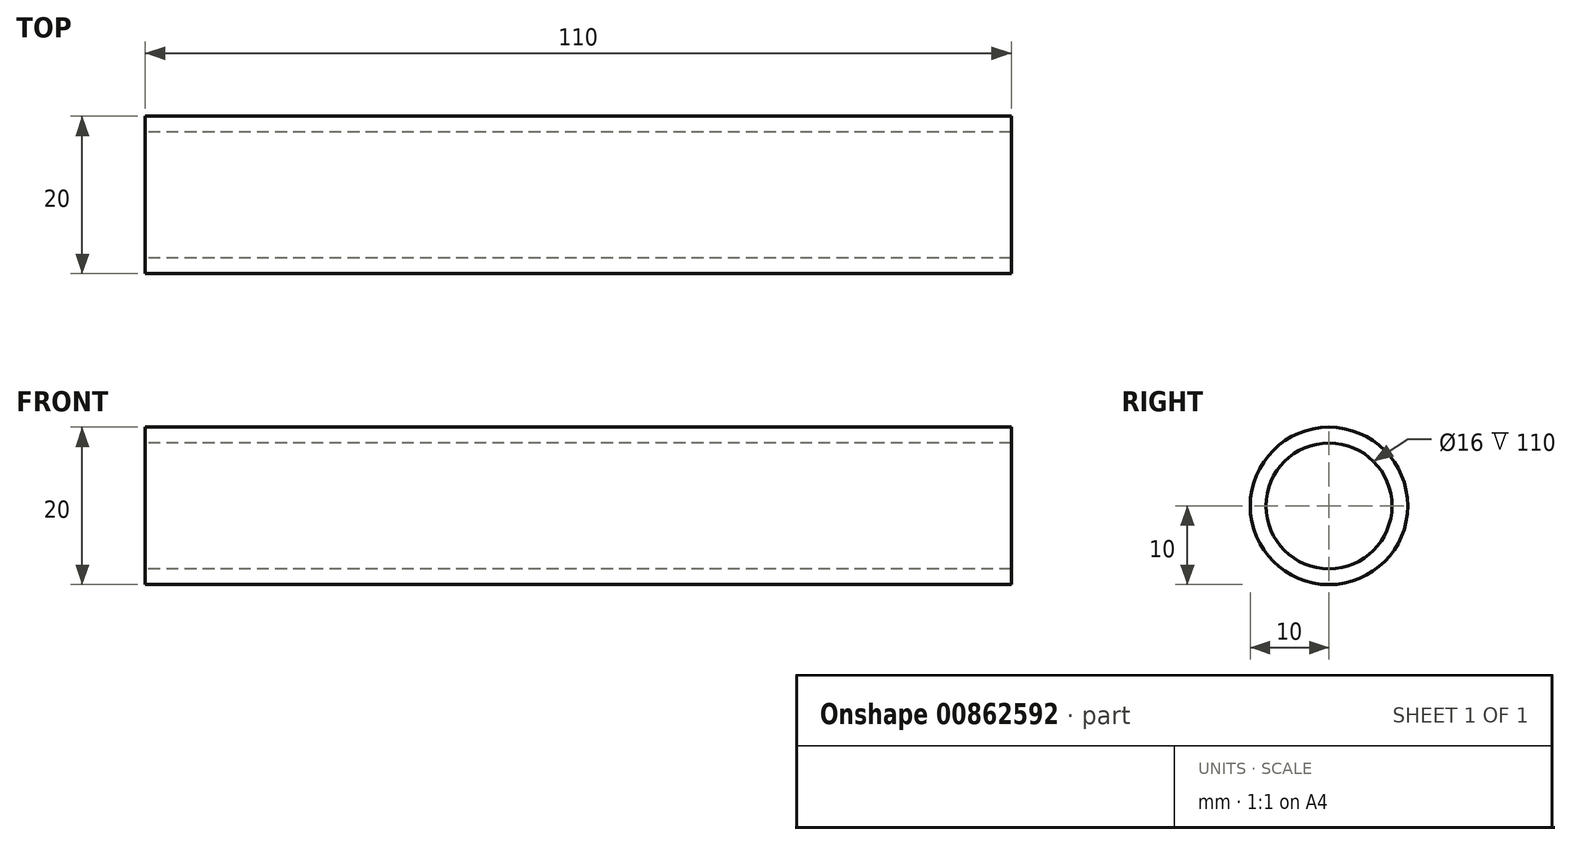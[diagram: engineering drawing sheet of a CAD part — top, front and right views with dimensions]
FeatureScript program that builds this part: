
annotation { "Feature Type Name" : "Feature", "Feature Type Description" : "" }
export const myFeature = defineFeature(function(context is Context, id is Id, definition is map)
    precondition{}
    {
        {
            var Q0;
            Q0=qCreatedBy(makeId("Front.planeOp"),FACE);
            var sketch = newSketch(context, id + "F0", { "sketchPlane" : qUnion([Q0])});
            skLineSegment(sketch, "E0", {"start": v(0, 0) * mm, "end": v(-110, 0) * mm});
            skSolve(sketch);
        }
        {
            var Q0;
            Q0=qCreatedBy(makeId("Right.planeOp"),FACE);
            var sketch = newSketch(context, id + "F1", { "sketchPlane" : qUnion([Q0])});
            skCircle(sketch, "E1", {"center": v(0, 0) * mm, "radius": 10 * mm});
            skCircle(sketch, "E2.0", {"center": v(0, 0) * mm, "radius": 8 * mm});
            skSolve(sketch);
        }
        {
            var Q0;
            Q0=makeQuery(id+"F1.imprint","IMPRINT",FACE,{"disambiguationData":[TD([[makeQuery(id+"F1.imprint","IMPRINT",EDGE,{"derivedFrom":sQuery(id+"F1.wireOp",EDGE,"E1")}),1.0]])]});
            var Q1;
            Q1=qSketchRegion(id+"F0",true);
            var Q2;
            Q2=sQuery(id+"F0.wireOp",EDGE,"E0");
            var Q3;
            Q3=sQuery(id+"F0.wireOp",EDGE,"p5A3UMdK-bUuJ-hKgG-gMdl-WLMVe5IsXQ4y");
            var Q4;
            Q4=sQuery(id+"F0.wireOp",EDGE,"jqzmJtes-IEFJ-0xae-phxS-a4aVOckqLKgL");
            sweep(context, id + "F2", {"profiles" : qUnion([Q0, Q1]), "path" : qUnion([Q2, Q3, Q4])});
        }
    });
